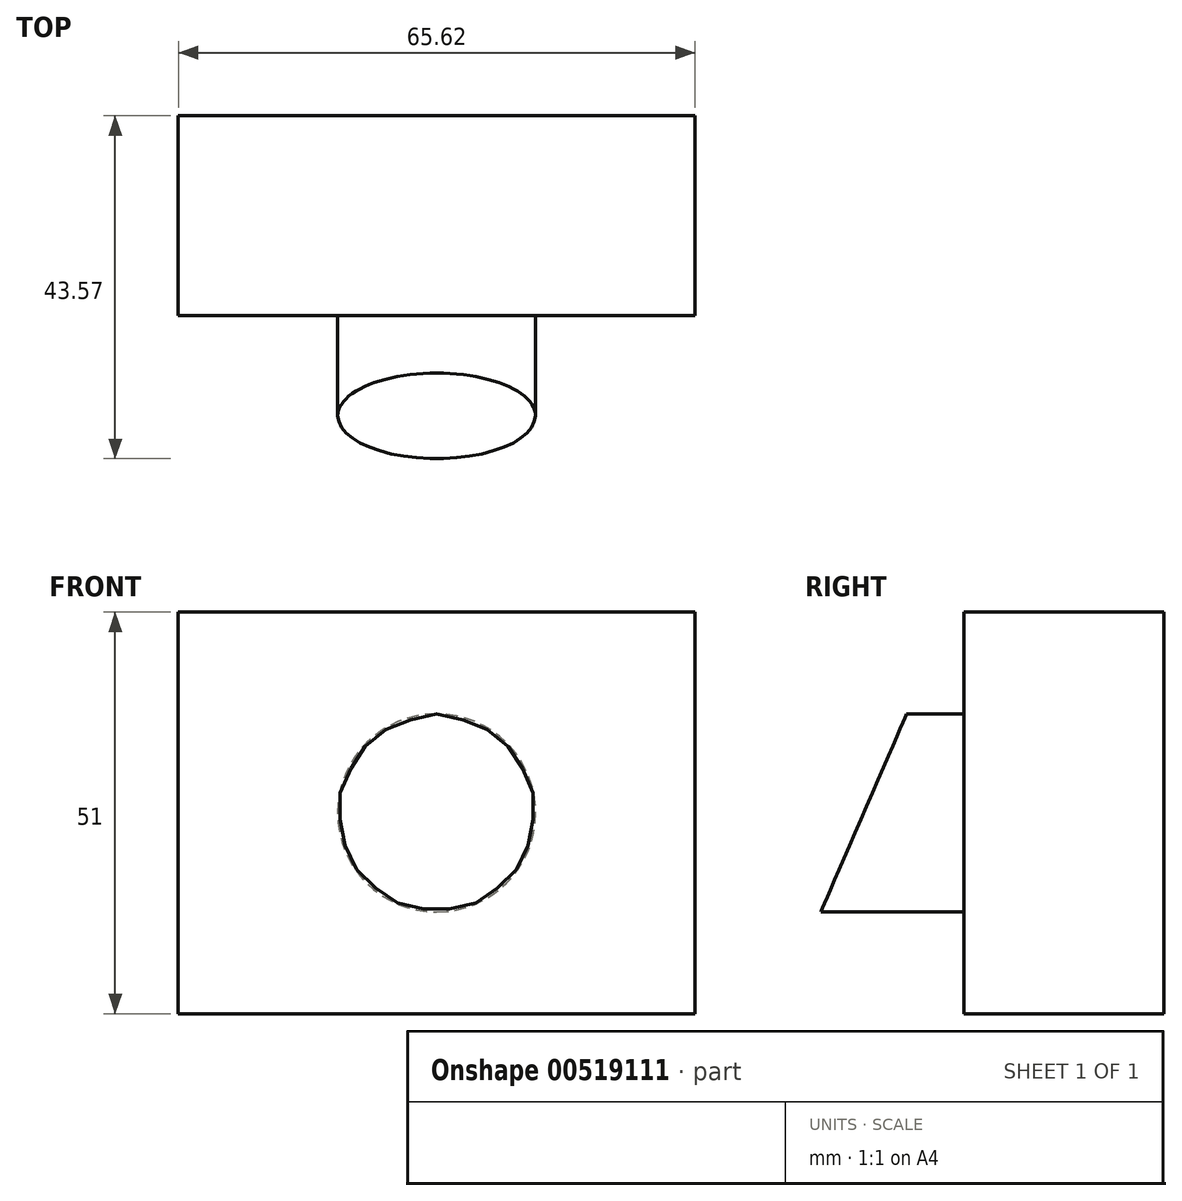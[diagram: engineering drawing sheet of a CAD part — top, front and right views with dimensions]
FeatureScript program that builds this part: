
annotation { "Feature Type Name" : "Feature", "Feature Type Description" : "" }
export const myFeature = defineFeature(function(context is Context, id is Id, definition is map)
    precondition{}
    {
        {
            var Q0;
            Q0=qCreatedBy(makeId("Front.planeOp"),FACE);
            var sketch = newSketch(context, id + "F0", { "sketchPlane" : qUnion([Q0])});
            skLineSegment(sketch, "E0.bottom", {"start": v(-32.81, 25.5) * mm, "end": v(32.81, 25.5) * mm});
            skLineSegment(sketch, "E0.top", {"start": v(-32.81, -25.5) * mm, "end": v(32.81, -25.5) * mm});
            skLineSegment(sketch, "E0.left", {"start": v(-32.81, 25.5) * mm, "end": v(-32.81, -25.5) * mm});
            skLineSegment(sketch, "E0.right", {"start": v(32.81, 25.5) * mm, "end": v(32.81, -25.5) * mm});
            skPoint(sketch, "E0.middle", {"position": v(0, 0) * mm});
            skSolve(sketch);
        }
        {
            var Q0;
            Q0 = qSketchRegion(id + "F0", true);
            extrude(context, id + "F1", {"entities" : qUnion([Q0]), "depth" : 25.4 * mm});
        }
        {
            var Q0;
            Q0=makeQuery(id+"F1.opExtrude","CAP_FACE",FACE,{"disambiguationData":[OSD([sQuery(id+"F0.wireOp",EDGE,"E0.bottom"),sQuery(id+"F0.wireOp",EDGE,"E0.top"),sQuery(id+"F0.wireOp",EDGE,"E0.left"),sQuery(id+"F0.wireOp",EDGE,"E0.right")])],"isStart":false});
            var sketch = newSketch(context, id + "F2", { "sketchPlane" : qUnion([Q0])});
            skCircle(sketch, "E1", {"center": v(0, 0) * mm, "radius": 12.58 * mm});
            skSolve(sketch);
        }
        {
            var Q0;
            Q0 = qSketchRegion(id + "F2", true);
            extrude(context, id + "F3", {"entities" : qUnion([Q0]), "operationType" : NewBodyOperationType.ADD, "depth" : 25.4 * mm});
        }
        {
            var Q0;
            Q0=qCreatedBy(makeId("Right.planeOp"),FACE);
            var sketch = newSketch(context, id + "F4", { "sketchPlane" : qUnion([Q0])});
            skLineSegment(sketch, "E2", {"start": v(-43.63, -12.73) * mm, "end": v(-32.53, 12.96) * mm});
            skLineSegment(sketch, "E3", {"start": v(-32.53, 12.96) * mm, "end": v(-51.24, 12.96) * mm});
            skLineSegment(sketch, "E4", {"start": v(-51.24, 12.96) * mm, "end": v(-51.24, -13.48) * mm});
            skLineSegment(sketch, "E5", {"start": v(-51.24, -13.48) * mm, "end": v(-43.63, -12.73) * mm});
            skSolve(sketch);
        }
        {
            var Q0;
            Q0 = qSketchRegion(id + "F4", true);
            extrude(context, id + "F5", {"entities" : qUnion([Q0]), "operationType" : NewBodyOperationType.REMOVE, "oppositeDirection" : true, "depth" : 25.4 * mm, "hasSecondDirection" : true, "secondDirectionOppositeDirection" : false, "secondDirectionDepth" : 25.4 * mm});
        }
    });
